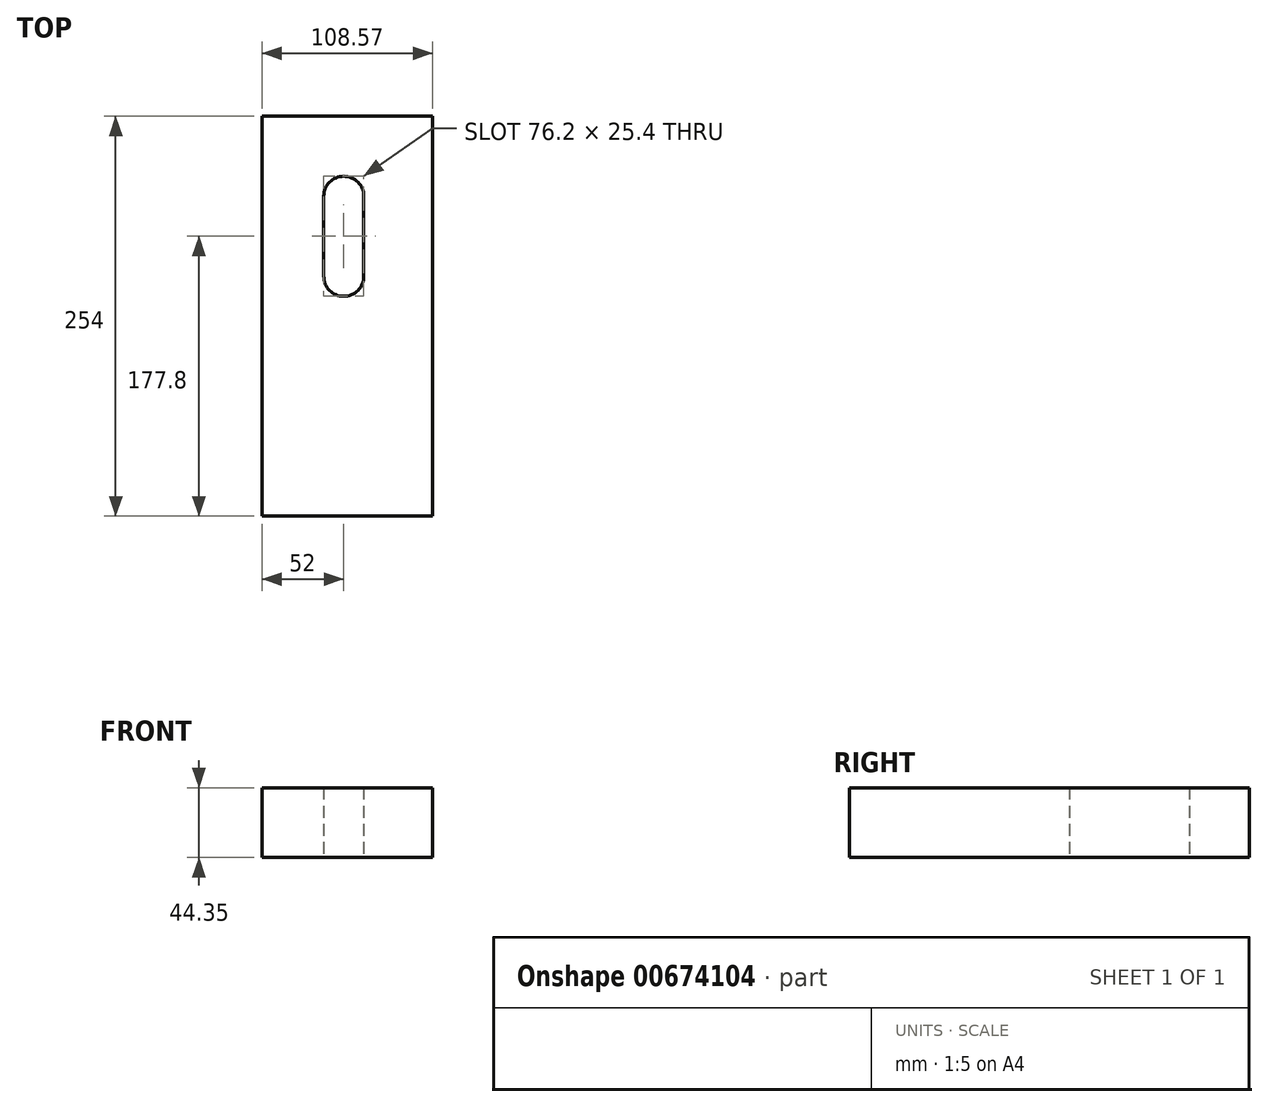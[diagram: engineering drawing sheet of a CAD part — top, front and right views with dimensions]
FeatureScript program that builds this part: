
annotation { "Feature Type Name" : "Feature", "Feature Type Description" : "" }
export const myFeature = defineFeature(function(context is Context, id is Id, definition is map)
    precondition{}
    {
        {
            var Q0;
            Q0=qCreatedBy(makeId("Front.planeOp"),FACE);
            var sketch = newSketch(context, id + "F0", { "sketchPlane" : qUnion([Q0])});
            skLineSegment(sketch, "E0.bottom", {"start": v(-52, 20.74) * mm, "end": v(56.57, 20.74) * mm});
            skLineSegment(sketch, "E0.top", {"start": v(-52, -23.6) * mm, "end": v(56.57, -23.6) * mm});
            skLineSegment(sketch, "E0.left", {"start": v(-52, 20.74) * mm, "end": v(-52, -23.6) * mm});
            skLineSegment(sketch, "E0.right", {"start": v(56.57, 20.74) * mm, "end": v(56.57, -23.6) * mm});
            skSolve(sketch);
        }
        {
            var Q0;
            Q0=makeQuery(id+"F0.imprint","IMPRINT",FACE,{"disambiguationData":[TD([[makeQuery(id+"F0.imprint","IMPRINT",EDGE,{"derivedFrom":sQuery(id+"F0.wireOp",EDGE,"E0.bottom")}),-1.0]])]});
            extrude(context, id + "F1", {"entities" : qUnion([Q0]), "depth" : 254 * mm, "offsetDistance" : 25.4 * mm});
        }
        {
            var Q0;
            Q0=makeQuery(id+"F1.opExtrude","SWEPT_FACE",FACE,{"disambiguationData":[OSD([sQuery(id+"F0.wireOp",EDGE,"E0.top")])]});
            var sketch = newSketch(context, id + "F2", { "sketchPlane" : qUnion([Q0])});
            skCircle(sketch, "E1", {"center": v(0, 50.8) * mm, "radius": 12.7 * mm});
            skCircle(sketch, "E2", {"center": v(0, 101.6) * mm, "radius": 12.7 * mm});
            skLineSegment(sketch, "E3.bottom", {"start": v(0, 50.8) * mm, "end": v(12.7, 50.8) * mm});
            skLineSegment(sketch, "E3.top", {"start": v(0, 101.6) * mm, "end": v(12.7, 101.6) * mm});
            skLineSegment(sketch, "E3.left", {"start": v(0, 50.8) * mm, "end": v(0, 101.6) * mm});
            skLineSegment(sketch, "E3.right", {"start": v(12.7, 50.8) * mm, "end": v(12.7, 101.6) * mm});
            skLineSegment(sketch, "E4.bottom", {"start": v(0, 50.8) * mm, "end": v(-12.7, 50.8) * mm});
            skLineSegment(sketch, "E4.top", {"start": v(0, 101.6) * mm, "end": v(-12.7, 101.6) * mm});
            skLineSegment(sketch, "E4.right", {"start": v(-12.7, 50.8) * mm, "end": v(-12.7, 101.6) * mm});
            skSolve(sketch);
        }
        {
            var Q0;
            Q0 = qSketchRegion(id + "F2", true);
            extrude(context, id + "F3", {"entities" : qUnion([Q0]), "operationType" : NewBodyOperationType.REMOVE, "oppositeDirection" : true, "depth" : 76.2 * mm, "offsetDistance" : 25.4 * mm});
        }
    });
